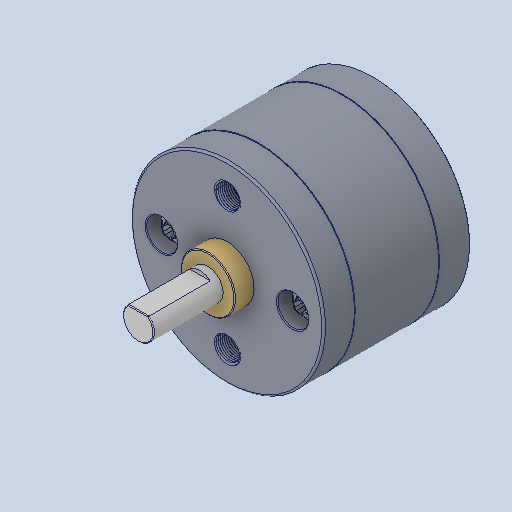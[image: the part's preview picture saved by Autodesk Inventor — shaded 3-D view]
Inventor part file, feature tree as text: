
AUTODESK INVENTOR PART (.ipt)
format: ipt  version: 2022 (Build 260153000, 153)  size: 711,168 bytes
history: mixed  units: mm
features: other x1, fillet x1, imported_body x1
ambient origin geometry x8: Origin, YZ Plane, XZ Plane, XY Plane, X Axis, Y Axis, Z Axis, Center Point
bodies: Body1 (imported_parasolid)
feature tree (3):
  other  "Твердое тело1"
  fillet  "Fillet2"  [1 undecoded]
  imported_body  NMx_Import_Brep_tag  [imported B-rep: ~6 faces, bbox_mm=None]
note: 1 required parameter value undecoded (feature->parameter linkage not recoverable at this tier; creation-order binding heuristic only, values carry confidence <= 0.55)
